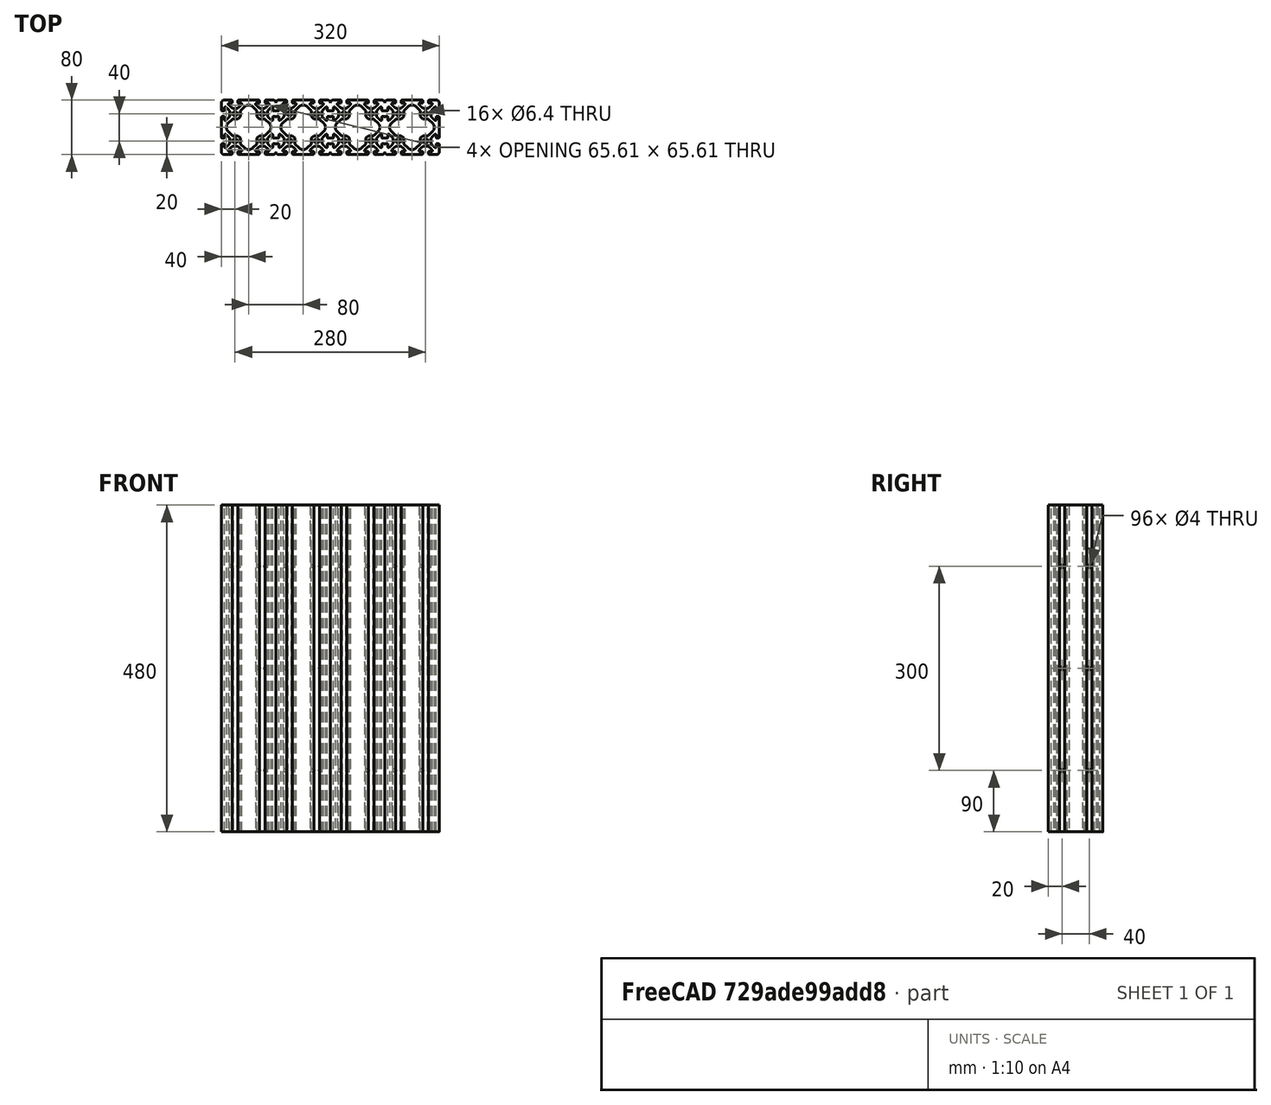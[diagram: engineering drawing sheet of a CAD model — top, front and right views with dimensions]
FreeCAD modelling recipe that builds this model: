
FCSTD DOCUMENT  (FreeCAD 0.21R38887 (Git))
Label: масивпрофілю
License: All rights reserved
LicenseURL: https://en.wikipedia.org/wiki/All_rights_reserved
objects: App::FeaturePython×2, Part::FeaturePython×2, App::Link×1, PartDesign::SubShapeBinder×1, PartDesign::LinearPattern×1, PartDesign::Body×1
note: 6 computed .brp shape members not serialized (recipe doc carries the construction recipe); baked Part::Feature solids carry a one-line shape summary decoded from their .brp
EXTERNAL_REF file=8080.FCStd obj=Body
EXTERNAL_REF file=ТаблицаПараметров.FCStd obj=Spreadsheet001

FEATURE [App::FeaturePython] Constraints  # WARN: FeaturePython — macro-defined, semantics opaque (R4)
  TreeRank = 37
  _LinkVersion = 1
  _Version = 1
FEATURE [App::FeaturePython] Elements  # WARN: FeaturePython — macro-defined, semantics opaque (R4)
  TreeRank = 38
  _LinkVersion = 1
FEATURE [App::Link] Link  label="Профиль80х80"
  AutoLinkLabel = false
  AutoPlacement = true
  LinkedObject = -> <external 8080.FCStd>#Body
  SyncGroupVisibility = false
  TreeRank = 40
  _LinkVersion = 1
FEATURE [PartDesign::SubShapeBinder] BaseFeature001  label="BaseFeature001(Профиль80х80)"
  BindCopyOnChange = 0
  BindMode = 0
  ClaimChildren = false
  Context = -> Assembly [Parts.Body.BaseFeature001.]
  EdgeTolerance = 1e-06
  FillStyle = 0
  Fuse = true
  InvalidShape = false
  MakeFace = true
  MergeEdges = true
  OffsetFill = false
  OffsetIntersection = false
  OffsetJoinType = 0
  OffsetOpenResult = false
  Outline = false
  PartialLoad = false
  Relative = true
  SplitEdges = false
  Support = -> [Link]
  TightBound = false
  TreeRank = 51
  ValidateShape = false
  _Version = 8
FEATURE [PartDesign::LinearPattern] LinearPattern
  AddSubType = 0
  BaseFeature = -> BaseFeature001
  CopyShape = false
  Direction = -> X_Axis
  InvalidShape = false
  Length = 240
  NewSolid = false
  Occurrences = 4
  OriginalSubs = -> [BaseFeature001]
  Originals = -> [BaseFeature001]
  ParallelTransform = true
  SubTransform = true
  Suppress = false
  TreeRank = 52
  ValidateShape = true
  _Version = 3
  expr: Length = ТаблицаПараметров#<<ТаблСтанина>>.GlubinaStaninu - ТаблицаПараметров#<<ТаблСтанина>>.RazmerProfilja
  expr: Occurrences = ТаблицаПараметров#<<ТаблСтанина>>.NumberProfileBody
FEATURE [PartDesign::Body] Body
  AutoGroupSolids = false
  BaseFeature = -> BaseFeature001
  ClaimAllChildren = false
  ExportMode = 0
  Group = -> [BaseFeature001,LinearPattern]
  InvalidShape = false
  Origin = -> Origin
  Tip = -> LinearPattern
  TreeRank = 50
  ValidateShape = false
  _ExportChildren = -> [BaseFeature001,LinearPattern]
  _GroupVersion = 1
FEATURE [Part::FeaturePython] Parts  # WARN: FeaturePython — macro-defined, semantics opaque (R4)
  Group = -> [Body]
  GroupMode = 0
  InvalidShape = false
  TreeRank = 39
  ValidateShape = false
  _LinkVersion = 1
FEATURE [Part::FeaturePython] Assembly  label="МасивПрофілю"  # WARN: FeaturePython — macro-defined, semantics opaque (R4)
  AutoRelax = true
  BuildShape = 0
  Freeze = false
  Group = -> [Constraints,Elements,Parts]
  InvalidShape = false
  TreeRank = 36
  ValidateShape = false
  Verbose = false
  _LinkVersion = 1
  _SolverType = 1
  _Version = 1
